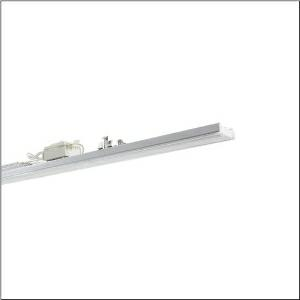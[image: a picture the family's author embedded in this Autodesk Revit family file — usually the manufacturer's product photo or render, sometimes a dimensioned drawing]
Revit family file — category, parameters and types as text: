
# Revit family: licross_r__11_recessed_extreme_mo_51te12dn49xge_aa6f
name_source: partatom
category: Lighting Fixtures
units: mm (PartAtom-declared; Revit-internal decimal feet)

## family parameters
Cut with Voids When Loaded = No
Host = Face
Light Source = No
Part Type = Normal
Room Calculation Point = No
Round Connector Dimension = Use Diameter
Shared = No

## types (1)
- --- (1 x LED, 9140 lm, 50.1 W, 4000K)
    Apparent Load = 50 VA
    CIE Flux Codes = 67 92 99 100 100
    Color Rendering = 80
    Color Temperature = 4000K
    Default Elevation = 1800 mm
    Description = Licross® 11 Recessed extreme MO, luminaire insert, of sheet steel, galvanised, coil coated, white, length: 1.500mm, width: 66mm, height: 67mm, LED rated luminous flux: 9.140lm, light colour: 840, control gear: DALI 2, with plug, 5-pole, with phase selection, mains connection: 220..240V, AC, 50/60Hz, rated input power: 50W, halogen-free wiring, primary optical cover: cover, of PMMA, light emission: direct distribution, primary light characteristic: symmetric, protection rating (complete): IP54, insulation class (complete): insulation class I (protective earthing), certification: CE, ENEC, VDE, UKCA, protection symbol: D if used in an environment with non-conductive dust loads with corresponding accessories, impact resistance: IK06, permissible ambient temperature for indoor applications: -25..+45°C, corresponds to IFS (International Featured Standards) requirements for safety and quality in the food industry, reducing of maximum allowable ambient temperature of 5°C with ceiling mounting, LABS conformity tested according to VDMA 24364:2018-05, packaging unit: 1 piece
    Height = 58 mm
    Lamp = 1 x LED
    Lamp Light Flux = 9140 lm
    Lamp Power = 50.1 W
    Lamp count = 1
    Length = 1500 mm
    Luminous efficacy = 182 lm/W
    Manufacturer = Siteco
    ModVariant = No
    Model = 51TE12DN49XGE
    Mounting Place = Ceiling
    Mounting Type = Pendant
    Number of Poles = 1
    OnlyDefault = Yes
    Power Factor = 1
    Product Name = Licross® 11 Recessed extreme MO
    Product group = luminaire insert
    ProductGroupID = 902
    Protection Class = Protection class I
    Protection Degree = IP 54
    RLX_Detail_Level = 1
    RLX_Emergency_Light_Flux = 0 lm
    RLX_Emergency_Type = 0
    RLX_Emergency_Type_DB = No
    RlxData = <blob elided: 24529 chars, md5=3298754d>
    Socket = socket
    Standby Power = 0 W
    System Light Flux = 9140 lm
    System Power = 50 W
    Type Comments = factory setting: luminous flux: 100 % | dim-lin: 254 | 334 mA
    Type Image = l_1296930.jpg
    URL = http://relux.com
    VarID = @adj_090352
    Voltage = 0 V
    Weight = 0.00 kg
    Width = 66 mm

## geometry (parser evidence)
native form markers: Blend x4, Sweep x9
no freeform markers — native parametric forms only
